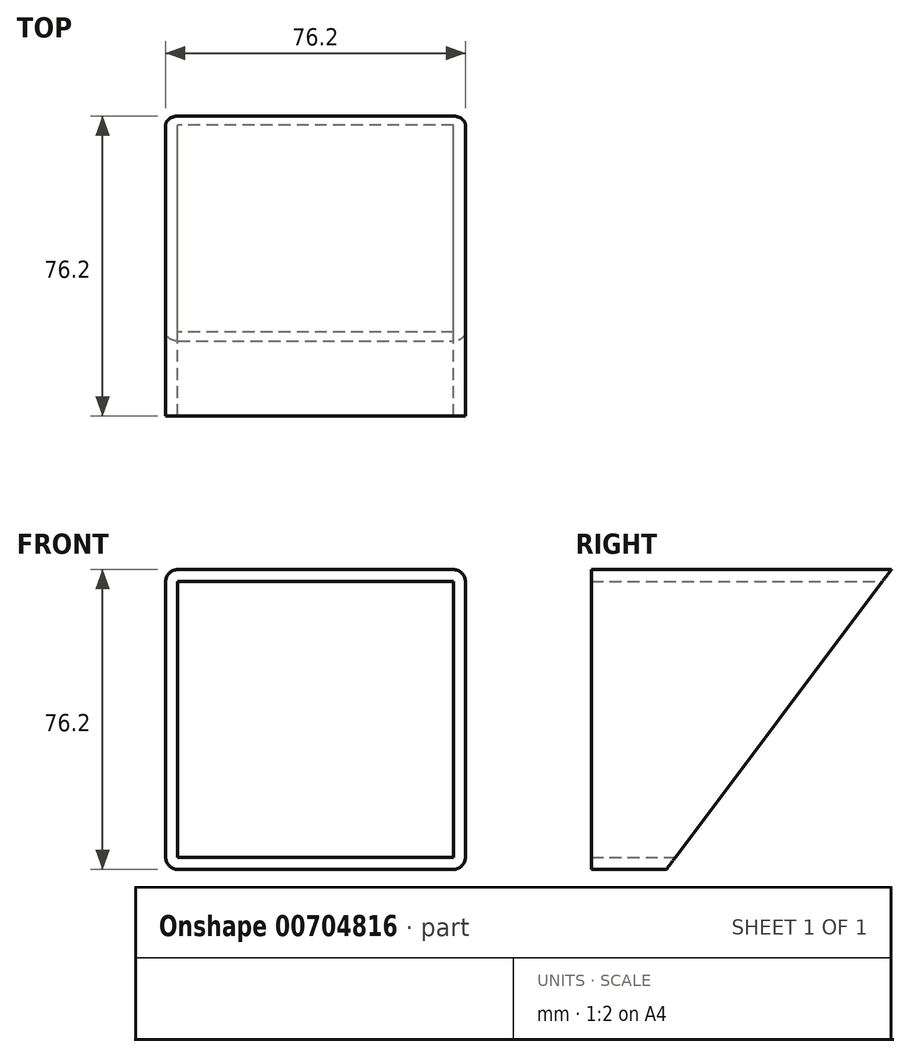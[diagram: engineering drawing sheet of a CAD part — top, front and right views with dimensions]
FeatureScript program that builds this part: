
annotation { "Feature Type Name" : "Feature", "Feature Type Description" : "" }
export const myFeature = defineFeature(function(context is Context, id is Id, definition is map)
    precondition{}
    {
        {
            var Q0;
            Q0=qCreatedBy(makeId("Front.planeOp"),FACE);
            var sketch = newSketch(context, id + "F0", { "sketchPlane" : qUnion([Q0])});
            skLineSegment(sketch, "E0.bottom", {"start": v(-38.1, 38.1) * mm, "end": v(38.1, 38.1) * mm});
            skLineSegment(sketch, "E0.top", {"start": v(-38.1, -38.1) * mm, "end": v(38.1, -38.1) * mm});
            skLineSegment(sketch, "E0.left", {"start": v(-38.1, 38.1) * mm, "end": v(-38.1, -38.1) * mm});
            skLineSegment(sketch, "E0.right", {"start": v(38.1, 38.1) * mm, "end": v(38.1, -38.1) * mm});
            skPoint(sketch, "E0.middle", {"position": v(0, 0) * mm});
            skPoint(sketch, "E1.visualSharp", {"position": v(-38.1, 38.1) * mm});
            skLineSegment(sketch, "E1.filletArc", {"start": v(-38.1, 38.1) * mm, "end": v(-38.1, 38.1) * mm});
            skPoint(sketch, "E2.visualSharp", {"position": v(38.1, 38.1) * mm});
            skLineSegment(sketch, "E2.filletArc", {"start": v(38.1, 38.1) * mm, "end": v(38.1, 38.1) * mm});
            skPoint(sketch, "E3.visualSharp", {"position": v(38.1, -38.1) * mm});
            skLineSegment(sketch, "E3.filletArc", {"start": v(38.1, -38.1) * mm, "end": v(38.1, -38.1) * mm});
            skPoint(sketch, "E4.visualSharp", {"position": v(-38.1, -38.1) * mm});
            skLineSegment(sketch, "E4.filletArc", {"start": v(-38.1, -38.1) * mm, "end": v(-38.1, -38.1) * mm});
            skLineSegment(sketch, "E5.0", {"start": v(-35.05, 35.05) * mm, "end": v(35.05, 35.05) * mm});
            skLineSegment(sketch, "E5.1", {"start": v(-35.05, 35.05) * mm, "end": v(-35.05, -35.05) * mm});
            skLineSegment(sketch, "E5.2", {"start": v(-35.05, -35.05) * mm, "end": v(35.05, -35.05) * mm});
            skLineSegment(sketch, "E5.3", {"start": v(35.05, 35.05) * mm, "end": v(35.05, -35.05) * mm});
            skSolve(sketch);
        }
        {
            var Q0;
            Q0=makeQuery(id+"F0.imprint","IMPRINT",FACE,{"disambiguationData":[TD([[makeQuery(id+"F0.imprint","IMPRINT",EDGE,{"derivedFrom":sQuery(id+"F0.wireOp",EDGE,"E0.bottom")}),-1.0]])]});
            extrude(context, id + "F1", {"entities" : qUnion([Q0]), "depth" : 241.3 * mm, "offsetDistance" : 25.4 * mm});
        }
        {
            var Q0;
            Q0=makeQuery(id+"F1.opExtrude","SWEPT_FACE",FACE,{"disambiguationData":[OSD([sQuery(id+"F0.wireOp",EDGE,"E0.right")])]});
            var sketch = newSketch(context, id + "F2", { "sketchPlane" : qUnion([Q0])});
            skLineSegment(sketch, "E6", {"start": v(-76.2, 38.1) * mm, "end": v(-76.2, -38.1) * mm});
            skLineSegment(sketch, "E7", {"start": v(-76.2, -38.1) * mm, "end": v(-57.15, -38.1) * mm});
            skLineSegment(sketch, "E8", {"start": v(-57.15, -38.1) * mm, "end": v(0, 38.1) * mm});
            skSolve(sketch);
        }
        {
            var Q0;
            {var subQ1=sQuery(id+"F0.wireOp",EDGE,"E0.right");var subQ2=makeQuery(id+"F1.opExtrude","CAP_EDGE",EDGE,{"disambiguationData":[OSD([subQ1])],"isStart":true});Q0=makeQuery(id+"F2.imprint","IMPRINT",FACE,{"disambiguationData":[TD([[makeQuery(id+"F2.imprint","IMPRINT",EDGE,{"derivedFrom":subQ2}),-1.0]])]});}
            extrude(context, id + "F3", {"entities" : qUnion([Q0]), "operationType" : NewBodyOperationType.REMOVE, "endBound" : BoundingType.THROUGH_ALL, "oppositeDirection" : true, "depth" : 25.4 * mm, "offsetDistance" : 25.4 * mm});
        }
        {
            var Q0;
            Q0=makeQuery(id+"F1.opExtrude","SWEPT_FACE",FACE,{"disambiguationData":[OSD([sQuery(id+"F0.wireOp",EDGE,"E0.right")])]});
            var sketch = newSketch(context, id + "F4", { "sketchPlane" : qUnion([Q0])});
            skLineSegment(sketch, "E9", {"start": v(-76.2, 38.1) * mm, "end": v(-76.2, -38.1) * mm});
            skSolve(sketch);
        }
        {
            var Q0;
            {var subQ0=sQuery(id+"F4.wireOp",EDGE,"E9");Q0=makeQuery(id+"F4.imprint","IMPRINT",FACE,{"disambiguationData":[TD([[makeQuery(id+"F4.imprint","IMPRINT",EDGE,{"derivedFrom":subQ0}),-1.0]])]});}
            extrude(context, id + "F5", {"entities" : qUnion([Q0]), "operationType" : NewBodyOperationType.REMOVE, "endBound" : BoundingType.THROUGH_ALL, "oppositeDirection" : true, "depth" : 25.4 * mm, "offsetDistance" : 25.4 * mm});
        }
        {
            var Q0;
            Q0=makeQuery(id+"F1.opExtrude","SWEPT_EDGE",EDGE,{"disambiguationData":[OSD([sQuery(id+"F0.wireOp",EDGE,"E0.bottom"),sQuery(id+"F0.wireOp",EDGE,"E0.right")])]});
            var Q1;
            Q1=makeQuery(id+"F1.opExtrude","SWEPT_EDGE",EDGE,{"disambiguationData":[OSD([sQuery(id+"F0.wireOp",EDGE,"E0.bottom"),sQuery(id+"F0.wireOp",EDGE,"E0.left")])]});
            var Q2;
            Q2=makeQuery(id+"F1.opExtrude","SWEPT_EDGE",EDGE,{"disambiguationData":[OSD([sQuery(id+"F0.wireOp",EDGE,"E0.top"),sQuery(id+"F0.wireOp",EDGE,"E0.left")])]});
            var Q3;
            Q3=makeQuery(id+"F1.opExtrude","SWEPT_EDGE",EDGE,{"disambiguationData":[OSD([sQuery(id+"F0.wireOp",EDGE,"E0.top"),sQuery(id+"F0.wireOp",EDGE,"E0.right")])]});
            fillet(context, id + "F6", {"entities" : qUnion([Q0, Q1, Q2, Q3]), "radius" : 3.17 * mm, "tangentPropagation" : true, "allowEdgeOverflow" : false});
        }
    });
